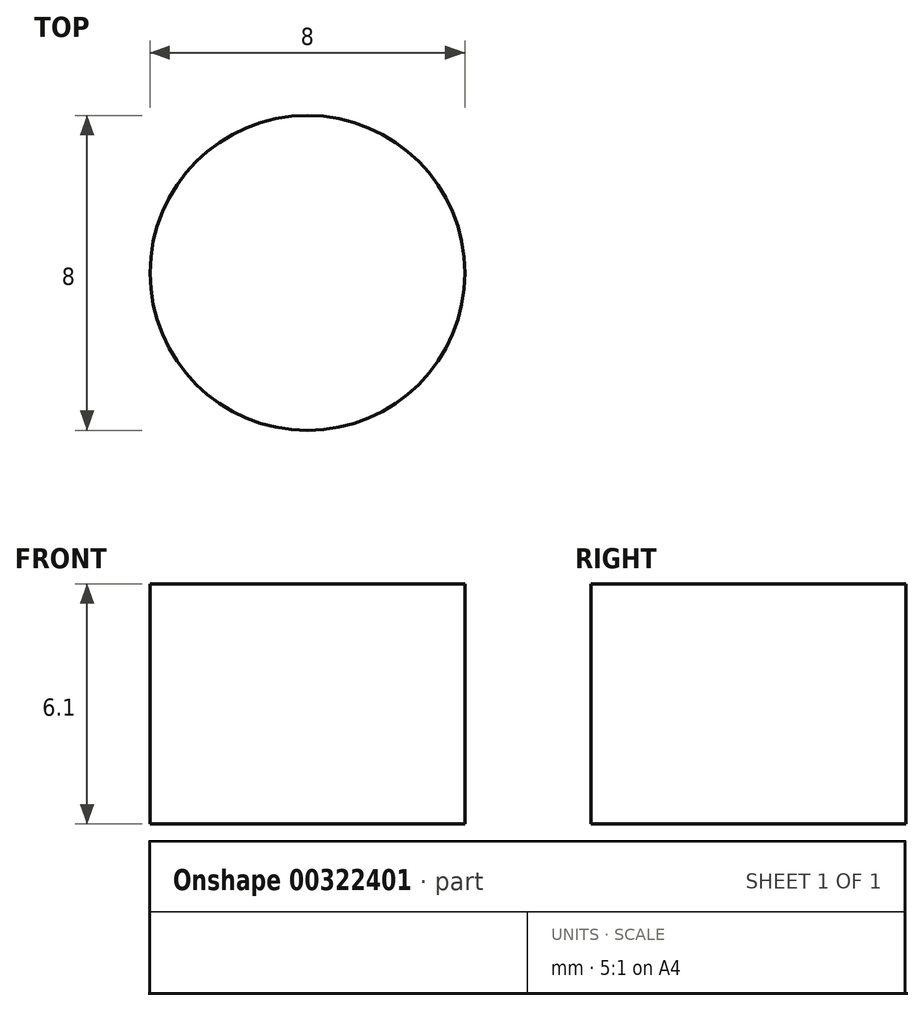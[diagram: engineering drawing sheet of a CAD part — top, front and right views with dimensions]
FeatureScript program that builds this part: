
annotation { "Feature Type Name" : "Feature", "Feature Type Description" : "" }
export const myFeature = defineFeature(function(context is Context, id is Id, definition is map)
    precondition{}
    {
        {
            var Q0;
            Q0=qCreatedBy(makeId("Top.planeOp"),FACE);
            var sketch = newSketch(context, id + "F0", { "sketchPlane" : qUnion([Q0])});
            skCircle(sketch, "E0", {"center": v(0, 0) * mm, "radius": 4 * mm});
            skSolve(sketch);
        }
        {
            var Q0;
            Q0 = qSketchRegion(id + "F0", true);
            extrude(context, id + "F1", {"entities" : qUnion([Q0]), "depth" : 6.1 * mm});
        }
    });
